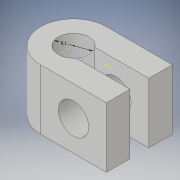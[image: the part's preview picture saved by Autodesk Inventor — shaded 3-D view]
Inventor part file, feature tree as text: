
AUTODESK INVENTOR PART (.ipt)
format: ipt  version: 2018 (Build 220112000, 112)  size: 140,800 bytes
history: native  units: in
note: dims shown in document units (in); Inventor stores cm internally (conversion verified against a paired STEP export)
features: sketch x12, extrude x4
ambient origin geometry x8: Origin, YZ Plane, XZ Plane, XY Plane, X Axis, Y Axis, Z Axis, Center Point
bodies: Body1 (feature_tree)
feature tree (16):
  sketch  "Sketch1"  dims[d0=0.3445in d1=0.3445in]
  sketch  "Sketch2"  dims[d2=0.689in d3=0.689in]
  sketch  "Sketch3"  dims[d7=0.3189in d9=0.1594in]
  sketch  "Sketch4"  dims[d10=0.6299in d11=0.0in d12=0.3189in]
  sketch  "Sketch5"  dims[d13=0.6299in d14=0.0in]
  extrude  "Extrusion2"  Depth=0.3445in
  sketch  "Sketch6"  dims[d15=0.3189in]
  sketch  "Sketch7"  dims[d16=0.6299in d17=0.0in]
  extrude  "Extrusion3"  Depth=0.689in
  extrude  "Extrusion4"  Depth=0.1594in
  sketch  "Sketch9"  dims[d19=0.1969in]
  sketch  "Sketch10"  dims[d20=0.2461in]
  sketch  "Sketch11"  dims[d21=0.6299in d22=0.0in]
  extrude  "Extrusion5"  Depth=0.6299in
  sketch  "Sketch8"  dims[d18=0.2461in]
  sketch  "Sketch12"
